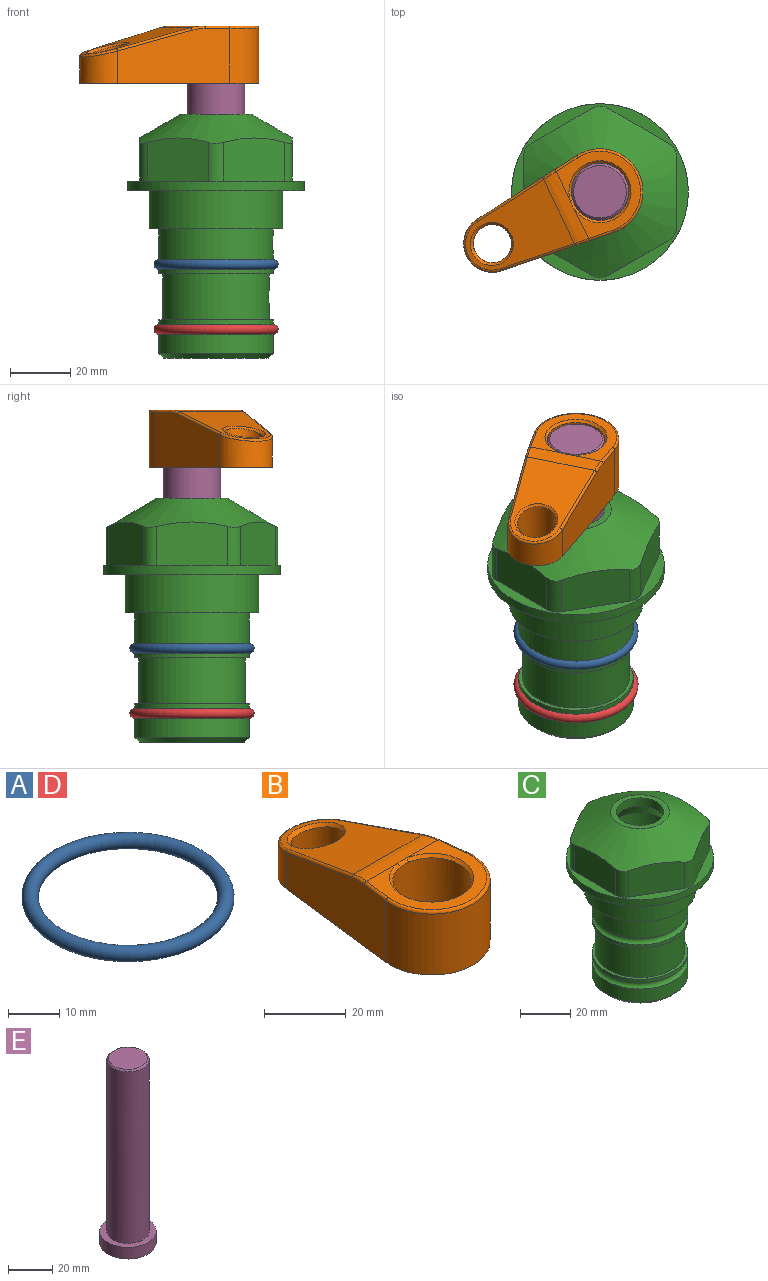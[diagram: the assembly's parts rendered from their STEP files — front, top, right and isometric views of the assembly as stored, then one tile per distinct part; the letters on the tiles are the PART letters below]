
ASSEMBLY  parts=5 mates=4
PART A: 1 faces, bbox 44.7x44.7x3.2 mm
  f0: torus R=19.05mm, axis (0,0,1), area 1193.9mm2
PART B: 31 faces, bbox 31.7x65.5x19.8 mm
  f0: plane 39.12x18.26mm, normal (0.99,0.12,0), area 612.2mm2, adj f1,f4,f7,f11,f13,f15
  f1: cylinder r=9.53mm len=18.91mm, axis (0,0,-1), area 296.1mm2, adj f0,f2,f7,f17
  f2: plane 39.12x18.26mm, normal (-0.99,0.12,0), area 612.2mm2, adj f1,f4,f7,f12,f14,f16
  f3: cylinder r=6.35mm len=12.7mm, axis (0,0,-1), area 362.4mm2, adj f7,f18
  f4: cylinder r=14.29mm len=28.58mm, axis (0,0,-1), area 882.2mm2, adj f0,f2,f7,f10
  f5: cylinder r=9.53mm len=19.05mm, axis (0,0,-1), area 1092.6mm2, adj f7,f19,f20
  f6: plane 26.99x23.69mm, normal (0,0,1), area 216.2mm2, adj f9,f10,f11,f12,f19
  f7: plane 63.5x28.58mm, normal (0,0,-1), area 661.8mm2, adj f0,f1,f2,f3,f4,f5,f22,f23
  f8: plane 33.52x23.6mm, normal (0,0.26,0.97), area 486mm2, adj f9,f15,f16,f17,f18
  f9: cylinder r=19.05mm len=24.72mm, axis (1,0,0), area 120.4mm2, adj f6,f8,f13,f14,f20
  f10: torus R=13.49mm, axis (0,0,1), area 59mm2, adj f4,f6,f11,f12
  f11: cylinder r=0.79mm len=8.67mm, axis (0.12,-0.99,0), area 10.8mm2, adj f0,f6,f10,f13
  f12: cylinder r=0.79mm len=8.67mm, axis (0.12,0.99,0), area 10.8mm2, adj f2,f6,f10,f14
  f13: bspline ~4.95x1.42mm, area 6.1mm2, adj f0,f9,f11,f15
  f14: bspline ~4.95x1.42mm, area 6.1mm2, adj f2,f9,f12,f16
  f15: cylinder r=0.79mm len=25.95mm, axis (0.12,-0.96,0.26), area 32.9mm2, adj f0,f8,f13,f17
  f16: cylinder r=0.79mm len=25.95mm, axis (0.12,0.96,-0.26), area 32.9mm2, adj f2,f8,f14,f17
  f17: bspline ~18.91x8.38mm, area 30mm2, adj f1,f8,f15,f16
  f18: bspline ~14.29x14.29mm, area 48.3mm2, adj f3,f8
  f19: cone r=9.53mm half-angle=45deg, axis (0,0,1), area 66.5mm2, adj f5,f6,f20
  f20: bspline ~3.22x0.96mm, area 3.5mm2, adj f5,f9,f19
  f21: plane 2.75x2.72mm, normal (0,0,-1), area 2.9mm2, adj f23,f25,f28
  f22: plane 23.05x15.88mm, normal (-0.99,-0.12,0), area 323.6mm2, adj f7,f25,f26,f27,f28,f29
  f23: plane 23.05x15.88mm, normal (0.99,-0.12,0), area 323.6mm2, adj f7,f21,f25,f27,f28,f30
  f24: cylinder r=9.53mm len=10.69mm, axis (0,0,-1), area 114.7mm2, adj f7,f27,f29,f30
  f25: cylinder r=12.7mm len=20.59mm, axis (0,0,-1), area 381.1mm2, adj f7,f21,f22,f23,f26,f28
  f26: plane 2.75x2.72mm, normal (0,0,-1), area 2.9mm2, adj f22,f25,f28
  f27: plane 19.72x18.37mm, normal (0,-0.26,-0.97), area 291.8mm2, adj f22,f23,f24,f28,f29,f30
  f28: cylinder r=15.88mm len=19.92mm, axis (1,0,0), area 54.8mm2, adj f21,f22,f23,f25,f26,f27
  f29: cylinder r=1.59mm len=11mm, axis (0,0,-1), area 34.7mm2, adj f7,f22,f24,f27
  f30: cylinder r=1.59mm len=11mm, axis (0,0,-1), area 34.7mm2, adj f7,f23,f24,f27
PART C: 36 faces, bbox 58.7x58.7x81 mm
  f0: cylinder r=17.78mm len=35.56mm, axis (0,0,1), area 1670.8mm2, adj f23,f24,f31
  f1: cylinder r=19.05mm len=38.1mm, axis (0,0,1), area 1191.9mm2, adj f26,f27,f30
  f2: plane 58.66x58.66mm, normal (0,0,-1), area 1150.6mm2, adj f3,f28
  f3: cylinder r=29.33mm len=58.66mm, axis (0,0,-1), area 585.1mm2, adj f2,f4
  f4: plane 58.66x58.66mm, normal (0,0,1), area 475.9mm2, adj f3,f5,f6,f7,f8,f9,f10,f11
  f5: plane 20.32x14.34mm, normal (-0.5,0.87,0), area 324.4mm2, adj f4,f15,f16,f17
  f6: plane 20.32x14.34mm, normal (0.5,0.87,0), area 324.4mm2, adj f4,f14,f15,f17
  f7: plane 23.48x14.34mm, normal (1,0,0), area 324.4mm2, adj f4,f13,f14,f17
  f8: plane 20.32x14.34mm, normal (0.5,-0.87,0), area 324.4mm2, adj f4,f12,f13,f17
  f9: plane 20.32x14.34mm, normal (-0.5,-0.87,0), area 324.4mm2, adj f4,f11,f12,f17
  f10: plane 23.48x14.34mm, normal (-1,0,0), area 324.4mm2, adj f4,f11,f16,f17
  f11: cylinder r=5.08mm len=12.85mm, axis (0,0,-1), area 67.2mm2, adj f4,f9,f10,f17
  f12: cylinder r=5.08mm len=12.85mm, axis (0,0,-1), area 67.2mm2, adj f4,f8,f9,f17
  f13: cylinder r=5.08mm len=12.85mm, axis (0,0,-1), area 67.2mm2, adj f4,f7,f8,f17
  f14: cylinder r=5.08mm len=12.85mm, axis (0,0,-1), area 67.2mm2, adj f4,f6,f7,f17
  f15: cylinder r=5.08mm len=12.85mm, axis (0,0,-1), area 67.2mm2, adj f4,f5,f6,f17
  f16: cylinder r=5.08mm len=12.85mm, axis (0,0,-1), area 67.2mm2, adj f4,f5,f10,f17
  f17: cone r=11.73mm half-angle=60deg, axis (0,0,-1), area 2071.8mm2, adj f5,f6,f7,f8,f9,f10,f11,f12
  f18: plane 23.46x23.46mm, normal (0,0,1), area 147.4mm2, adj f17,f35
  f19: plane 34.93x34.93mm, normal (0,0,-1), area 958mm2, adj f29
  f20: cylinder r=19.05mm len=38.1mm, axis (0,0,1), area 760.1mm2, adj f21,f29
  f21: torus R=19.05mm, axis (0,0,1), area 565.3mm2, adj f20,f22
  f22: cylinder r=19.05mm len=38.1mm, axis (0,0,1), area 190mm2, adj f21,f23
  f23: plane 38.1x38.1mm, normal (0,0,1), area 146.9mm2, adj f0,f22
  f24: plane 38.1x38.1mm, normal (0,0,-1), area 146.9mm2, adj f0,f25
  f25: cylinder r=19.05mm len=38.1mm, axis (0,0,1), area 190mm2, adj f24,f26
  f26: torus R=19.05mm, axis (0,0,1), area 565.3mm2, adj f1,f25
  f27: plane 44.45x44.45mm, normal (0,0,-1), area 411.7mm2, adj f1,f28
  f28: cylinder r=22.23mm len=44.45mm, axis (0,0,1), area 1773.5mm2, adj f2,f27
  f29: cone r=19.05mm half-angle=45deg, axis (0,0,1), area 257.5mm2, adj f19,f20
  f30: cylinder r=3.17mm len=6.75mm, axis (-1,0,0), area 128mm2, adj f1,f33
  f31: cylinder r=3.17mm len=6.35mm, axis (-1,0,0), area 102.5mm2, adj f0,f33
  f32: plane 25.4x25.4mm, normal (0,0,1), area 506.7mm2, adj f33
  f33: cylinder r=12.7mm len=66.42mm, axis (0,0,-1), area 5236.2mm2, adj f30,f31,f32,f34
  f34: cone r=9.53mm half-angle=30deg, axis (0,0,-1), area 443.4mm2, adj f33,f35
  f35: cylinder r=9.53mm len=19.05mm, axis (0,0,-1), area 240.9mm2, adj f18,f34
PART D: same geometry as A
PART E: 6 faces, bbox 25.4x25.4x101.6 mm
  f0: plane 17.46x17.46mm, normal (0,0,1), area 239.5mm2, adj f5
  f1: plane 25.4x25.4mm, normal (0,0,-1), area 506.7mm2, adj f2
  f2: cylinder r=12.7mm len=25.4mm, axis (0,0,1), area 506.7mm2, adj f1,f3
  f3: plane 25.4x25.4mm, normal (0,0,1), area 221.7mm2, adj f2,f4
  f4: cylinder r=9.53mm len=94.46mm, axis (0,0,1), area 5653mm2, adj f3,f5
  f5: cone r=8.73mm half-angle=45deg, axis (0,0,-1), area 64.4mm2, adj f0,f4
PLACE A at identity
PLACE B rot(axis=(0,0,1),115.7deg) t=(0,0,-8.79)mm
PLACE C at identity fixed
PLACE D t=(0,0,-21.59)mm
PLACE E rot(axis=(0,0,1),115.7deg) t=(0,0,-9.59)mm
MATE fastened D.f0 <-> C.f0  axis (0,0,1) through (0,0,-46.1)mm
MATE fastened E.f2 <-> B.f4  axis (0,0,1) through (0,0,53.91)mm
MATE cylindrical E.f2 <-> C.f0  axis (0,0,-1) through (0,0,-47.69)mm
MATE fastened A.f0 <-> C.f0  axis (0,0,1) through (0,0,-24.51)mm
